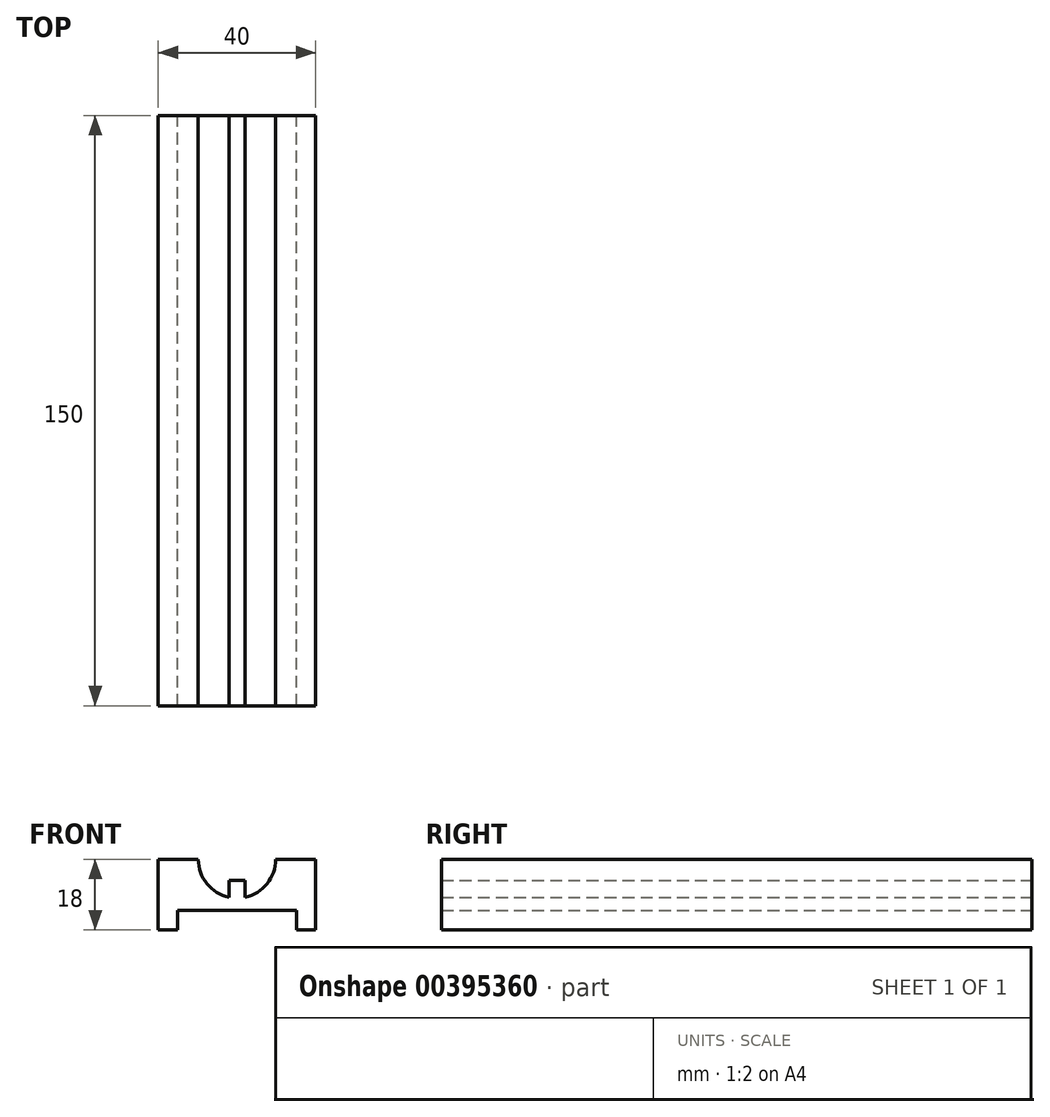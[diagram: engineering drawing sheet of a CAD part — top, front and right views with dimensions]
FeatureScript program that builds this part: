
annotation { "Feature Type Name" : "Feature", "Feature Type Description" : "" }
export const myFeature = defineFeature(function(context is Context, id is Id, definition is map)
    precondition{}
    {
        {
            var Q0;
            Q0=qCreatedBy(makeId("Front.planeOp"),FACE);
            var sketch = newSketch(context, id + "F0", { "sketchPlane" : qUnion([Q0])});
            skLineSegment(sketch, "E0.top", {"start": v(20, -18) * mm, "end": v(15.1, -18) * mm});
            skLineSegment(sketch, "E0.left", {"start": v(20, 0) * mm, "end": v(20, -18) * mm});
            skLineSegment(sketch, "E0.right", {"start": v(-20, 0) * mm, "end": v(-20, -18) * mm});
            skPoint(sketch, "E0.middle", {"position": v(0, 0) * mm});
            skLineSegment(sketch, "E1.top", {"start": v(-15.1, -13) * mm, "end": v(15.1, -13) * mm});
            skLineSegment(sketch, "E1.left", {"start": v(-15.1, -18) * mm, "end": v(-15.1, -13) * mm});
            skLineSegment(sketch, "E1.right", {"start": v(15.1, -18) * mm, "end": v(15.1, -13) * mm});
            skLineSegment(sketch, "E2.trimOffspring", {"start": v(-15.1, -18) * mm, "end": v(-20, -18) * mm});
            skArc(sketch, "E3", {"start": v(2.05, -9.63) * mm, "mid": v(7.65, -6.2) * mm, "end": v(9.85, 0) * mm});
            skLineSegment(sketch, "E4.top", {"start": v(2.05, -5.35) * mm, "end": v(-2.05, -5.35) * mm});
            skLineSegment(sketch, "E4.left", {"start": v(2.05, -9.63) * mm, "end": v(2.05, -5.35) * mm});
            skLineSegment(sketch, "E4.right", {"start": v(-2.05, -9.63) * mm, "end": v(-2.05, -5.35) * mm});
            skArc(sketch, "E5.trimOffspring", {"start": v(-9.85, 0) * mm, "mid": v(-7.65, -6.2) * mm, "end": v(-2.05, -9.63) * mm});
            skLineSegment(sketch, "E6", {"start": v(-20, 0) * mm, "end": v(-9.85, 0) * mm});
            skLineSegment(sketch, "E7.trimOffspring", {"start": v(9.85, 0) * mm, "end": v(20, 0) * mm});
            skPoint(sketch, "E8.trimOffspring.end.orphan", {"position": v(-20, 18) * mm});
            skPoint(sketch, "E9.top.start.orphan", {"position": v(-15.1, 17) * mm});
            skPoint(sketch, "E9.right.end.orphan", {"position": v(15.1, 15) * mm});
            skPoint(sketch, "E10.orphan", {"position": v(20, 18) * mm});
            skPoint(sketch, "E11.top.start.orphan", {"position": v(-2.05, 4.35) * mm});
            skSolve(sketch);
        }
        {
            var Q0;
            Q0=qSketchRegion(id+"F0",true);
            extrude(context, id + "F1", {"entities" : qUnion([Q0]), "depth" : 150 * mm});
        }
    });
